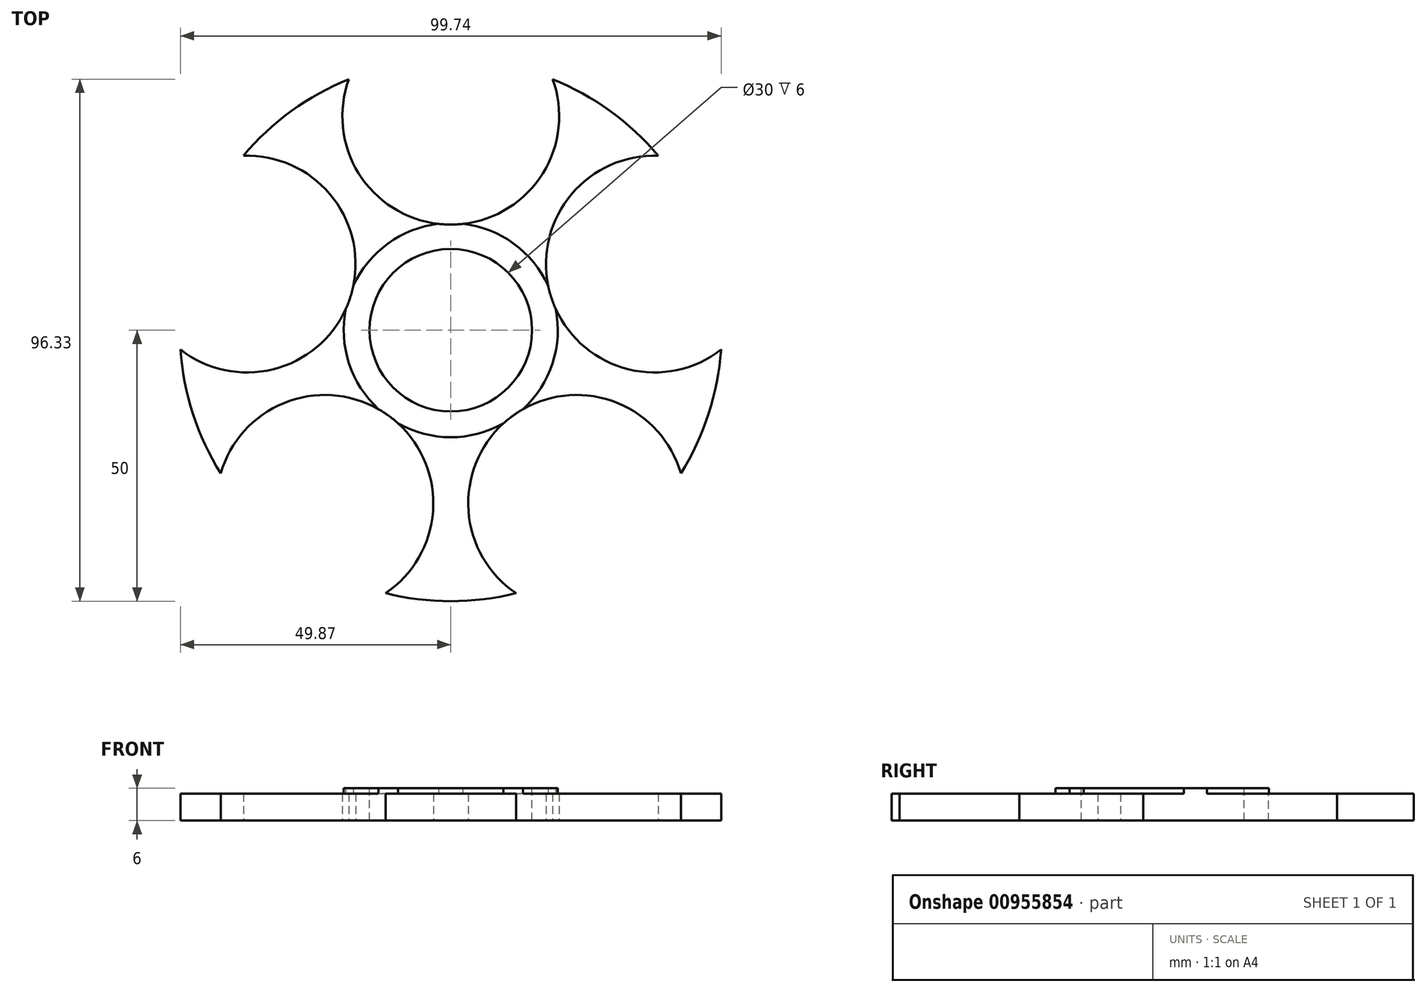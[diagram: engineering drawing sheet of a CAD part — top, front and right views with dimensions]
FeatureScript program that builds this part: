
annotation { "Feature Type Name" : "Feature", "Feature Type Description" : "" }
export const myFeature = defineFeature(function(context is Context, id is Id, definition is map)
    precondition{}
    {
        {
            var Q0;
            Q0=qCreatedBy(makeId("Top.planeOp"),FACE);
            var sketch = newSketch(context, id + "F0", { "sketchPlane" : qUnion([Q0])});
            skCircle(sketch, "E0.cCircle", {"center": v(0, 0) * mm, "radius": 39.5 * mm, "construction": true});
            skLineSegment(sketch, "E0.0", {"start": v(37.57, 12.2) * mm, "end": v(23.22, -31.96) * mm});
            skLineSegment(sketch, "E0.1", {"start": v(23.22, -31.96) * mm, "end": v(-23.22, -31.96) * mm});
            skLineSegment(sketch, "E0.2", {"start": v(-23.22, -31.96) * mm, "end": v(-37.57, 12.2) * mm});
            skLineSegment(sketch, "E0.3", {"start": v(-37.57, 12.2) * mm, "end": v(0, 39.5) * mm});
            skLineSegment(sketch, "E0.4", {"start": v(0, 39.5) * mm, "end": v(37.57, 12.2) * mm});
            skCircle(sketch, "E1", {"center": v(0, 39.5) * mm, "radius": 20 * mm});
            skCircle(sketch, "E2", {"center": v(37.57, 12.2) * mm, "radius": 20 * mm});
            skCircle(sketch, "E3", {"center": v(0, 0) * mm, "radius": 60 * mm});
            skCircle(sketch, "E4", {"center": v(-23.22, -31.96) * mm, "radius": 20 * mm});
            skCircle(sketch, "E5", {"center": v(23.22, -31.96) * mm, "radius": 20 * mm});
            skCircle(sketch, "E6", {"center": v(-37.57, 12.2) * mm, "radius": 20 * mm});
            skSolve(sketch);
        }
        {
            var Q0;
            Q0=makeQuery(id+"F0.imprint","IMPRINT",FACE,{"disambiguationData":[TD([[makeQuery(id+"F0.imprint","IMPRINT",EDGE,{"derivedFrom":sQuery(id+"F0.wireOp",EDGE,"E3")}),1.0]])]});
            var Q1;
            {var subQ0=sQuery(id+"F0.wireOp",EDGE,"E0.3");var subQ1=sQuery(id+"F0.wireOp",EDGE,"E0.2");var subQ2=makeQuery(id+"F0.imprint","INTERSECT",VERTEX,{"derivedFrom":[subQ1,subQ0]});Q1=makeQuery(id+"F0.imprint","IMPRINT",FACE,{"disambiguationData":[TD([[makeQuery(id+"F0.imprint","IMPRINT",EDGE,{"disambiguationData":[TD([[subQ2,1.0]])],"derivedFrom":subQ1}),1.0]])]});}
            var Q2;
            {var subQ0=sQuery(id+"F0.wireOp",EDGE,"E0.3");var subQ1=sQuery(id+"F0.wireOp",EDGE,"E0.2");var subQ2=makeQuery(id+"F0.imprint","INTERSECT",VERTEX,{"derivedFrom":[subQ1,subQ0]});Q2=makeQuery(id+"F0.imprint","IMPRINT",FACE,{"disambiguationData":[TD([[makeQuery(id+"F0.imprint","IMPRINT",EDGE,{"disambiguationData":[TD([[subQ2,1.0]])],"derivedFrom":subQ1}),-1.0]])]});}
            var Q3;
            {var subQ0=sQuery(id+"F0.wireOp",EDGE,"E0.2");var subQ1=sQuery(id+"F0.wireOp",EDGE,"E0.1");var subQ2=makeQuery(id+"F0.imprint","INTERSECT",VERTEX,{"derivedFrom":[subQ1,subQ0]});Q3=makeQuery(id+"F0.imprint","IMPRINT",FACE,{"disambiguationData":[TD([[makeQuery(id+"F0.imprint","IMPRINT",EDGE,{"disambiguationData":[TD([[subQ2,1.0]])],"derivedFrom":subQ1}),1.0]])]});}
            var Q4;
            {var subQ0=sQuery(id+"F0.wireOp",EDGE,"E0.2");var subQ1=sQuery(id+"F0.wireOp",EDGE,"E0.1");var subQ2=makeQuery(id+"F0.imprint","INTERSECT",VERTEX,{"derivedFrom":[subQ1,subQ0]});Q4=makeQuery(id+"F0.imprint","IMPRINT",FACE,{"disambiguationData":[TD([[makeQuery(id+"F0.imprint","IMPRINT",EDGE,{"disambiguationData":[TD([[subQ2,1.0]])],"derivedFrom":subQ1}),-1.0]])]});}
            var Q5;
            {var subQ0=sQuery(id+"F0.wireOp",EDGE,"E0.1");var subQ1=sQuery(id+"F0.wireOp",EDGE,"E0.0");var subQ2=makeQuery(id+"F0.imprint","INTERSECT",VERTEX,{"derivedFrom":[subQ1,subQ0]});Q5=makeQuery(id+"F0.imprint","IMPRINT",FACE,{"disambiguationData":[TD([[makeQuery(id+"F0.imprint","IMPRINT",EDGE,{"disambiguationData":[TD([[subQ2,1.0]])],"derivedFrom":subQ1}),1.0]])]});}
            var Q6;
            {var subQ0=sQuery(id+"F0.wireOp",EDGE,"E0.1");var subQ1=sQuery(id+"F0.wireOp",EDGE,"E0.0");var subQ2=makeQuery(id+"F0.imprint","INTERSECT",VERTEX,{"derivedFrom":[subQ1,subQ0]});Q6=makeQuery(id+"F0.imprint","IMPRINT",FACE,{"disambiguationData":[TD([[makeQuery(id+"F0.imprint","IMPRINT",EDGE,{"disambiguationData":[TD([[subQ2,1.0]])],"derivedFrom":subQ1}),-1.0]])]});}
            var Q7;
            {var subQ15=sQuery(id+"F0.wireOp",EDGE,"E2");var subQ16=sQuery(id+"F0.wireOp",EDGE,"E0.0");var subQ17=makeQuery(id+"F0.imprint","INTERSECT",VERTEX,{"derivedFrom":[subQ16,subQ15]});Q7=makeQuery(id+"F0.imprint","IMPRINT",FACE,{"disambiguationData":[TD([[makeQuery(id+"F0.imprint","IMPRINT",EDGE,{"disambiguationData":[TD([[subQ17,-1.0]])],"derivedFrom":subQ16}),-1.0]])]});}
            var Q8;
            {var subQ0=sQuery(id+"F0.wireOp",EDGE,"E0.4");var subQ1=sQuery(id+"F0.wireOp",EDGE,"E0.0");var subQ2=makeQuery(id+"F0.imprint","INTERSECT",VERTEX,{"derivedFrom":[subQ1,subQ0]});Q8=makeQuery(id+"F0.imprint","IMPRINT",FACE,{"disambiguationData":[TD([[makeQuery(id+"F0.imprint","IMPRINT",EDGE,{"disambiguationData":[TD([[subQ2,-1.0]])],"derivedFrom":subQ1}),-1.0]])]});}
            var Q9;
            {var subQ0=sQuery(id+"F0.wireOp",EDGE,"E0.4");var subQ1=sQuery(id+"F0.wireOp",EDGE,"E0.0");var subQ2=makeQuery(id+"F0.imprint","INTERSECT",VERTEX,{"derivedFrom":[subQ1,subQ0]});Q9=makeQuery(id+"F0.imprint","IMPRINT",FACE,{"disambiguationData":[TD([[makeQuery(id+"F0.imprint","IMPRINT",EDGE,{"disambiguationData":[TD([[subQ2,-1.0]])],"derivedFrom":subQ1}),1.0]])]});}
            var Q10;
            {var subQ0=sQuery(id+"F0.wireOp",EDGE,"E0.4");var subQ1=sQuery(id+"F0.wireOp",EDGE,"E0.3");var subQ2=makeQuery(id+"F0.imprint","INTERSECT",VERTEX,{"derivedFrom":[subQ1,subQ0]});Q10=makeQuery(id+"F0.imprint","IMPRINT",FACE,{"disambiguationData":[TD([[makeQuery(id+"F0.imprint","IMPRINT",EDGE,{"disambiguationData":[TD([[subQ2,1.0]])],"derivedFrom":subQ1}),-1.0]])]});}
            var Q11;
            {var subQ0=sQuery(id+"F0.wireOp",EDGE,"E0.4");var subQ1=sQuery(id+"F0.wireOp",EDGE,"E0.3");var subQ2=makeQuery(id+"F0.imprint","INTERSECT",VERTEX,{"derivedFrom":[subQ1,subQ0]});Q11=makeQuery(id+"F0.imprint","IMPRINT",FACE,{"disambiguationData":[TD([[makeQuery(id+"F0.imprint","IMPRINT",EDGE,{"disambiguationData":[TD([[subQ2,1.0]])],"derivedFrom":subQ1}),1.0]])]});}
            extrude(context, id + "F1", {"entities" : qUnion([Q0, Q1, Q2, Q3, Q4, Q5, Q6, Q7, Q8, Q9, Q10, Q11]), "depth" : 5 * mm, "offsetDistance" : 25 * mm});
        }
        {
            var Q0;
            Q0=makeQuery(id+"F1.opExtrude","CAP_FACE",FACE,{"disambiguationData":[OSD([sQuery(id+"F0.wireOp",EDGE,"E3")])],"isStart":false});
            var sketch = newSketch(context, id + "F2", { "sketchPlane" : qUnion([Q0])});
            skCircle(sketch, "E7", {"center": v(0, 0) * mm, "radius": 19.75 * mm});
            skSolve(sketch);
        }
        {
            var Q0;
            Q0=makeQuery(id+"F2.imprint","IMPRINT",FACE,{"disambiguationData":[TD([[makeQuery(id+"F2.imprint","IMPRINT",EDGE,{"derivedFrom":sQuery(id+"F2.wireOp",EDGE,"E7")}),1.0]])]});
            extrude(context, id + "F3", {"entities" : qUnion([Q0]), "operationType" : NewBodyOperationType.ADD, "depth" : 1 * mm, "offsetDistance" : 25 * mm});
        }
        {
            var Q0;
            {var subQ0=sQuery(id+"F0.wireOp",EDGE,"E0.2");var subQ1=sQuery(id+"F0.wireOp",EDGE,"E0.1");var subQ2=makeQuery(id+"F0.imprint","INTERSECT",VERTEX,{"derivedFrom":[subQ1,subQ0]});Q0=makeQuery(id+"F0.imprint","IMPRINT",FACE,{"disambiguationData":[TD([[makeQuery(id+"F0.imprint","IMPRINT",EDGE,{"disambiguationData":[TD([[subQ2,1.0]])],"derivedFrom":subQ1}),1.0]])]});}
            var Q1;
            {var subQ0=sQuery(id+"F0.wireOp",EDGE,"E0.2");var subQ1=sQuery(id+"F0.wireOp",EDGE,"E0.1");var subQ2=makeQuery(id+"F0.imprint","INTERSECT",VERTEX,{"derivedFrom":[subQ1,subQ0]});Q1=makeQuery(id+"F0.imprint","IMPRINT",FACE,{"disambiguationData":[TD([[makeQuery(id+"F0.imprint","IMPRINT",EDGE,{"disambiguationData":[TD([[subQ2,1.0]])],"derivedFrom":subQ1}),-1.0]])]});}
            var Q2;
            {var subQ0=sQuery(id+"F0.wireOp",EDGE,"E0.1");var subQ1=sQuery(id+"F0.wireOp",EDGE,"E0.0");var subQ2=makeQuery(id+"F0.imprint","INTERSECT",VERTEX,{"derivedFrom":[subQ1,subQ0]});Q2=makeQuery(id+"F0.imprint","IMPRINT",FACE,{"disambiguationData":[TD([[makeQuery(id+"F0.imprint","IMPRINT",EDGE,{"disambiguationData":[TD([[subQ2,1.0]])],"derivedFrom":subQ1}),1.0]])]});}
            var Q3;
            {var subQ0=sQuery(id+"F0.wireOp",EDGE,"E0.1");var subQ1=sQuery(id+"F0.wireOp",EDGE,"E0.0");var subQ2=makeQuery(id+"F0.imprint","INTERSECT",VERTEX,{"derivedFrom":[subQ1,subQ0]});Q3=makeQuery(id+"F0.imprint","IMPRINT",FACE,{"disambiguationData":[TD([[makeQuery(id+"F0.imprint","IMPRINT",EDGE,{"disambiguationData":[TD([[subQ2,1.0]])],"derivedFrom":subQ1}),-1.0]])]});}
            var Q4;
            {var subQ0=sQuery(id+"F0.wireOp",EDGE,"E0.4");var subQ1=sQuery(id+"F0.wireOp",EDGE,"E0.0");var subQ2=makeQuery(id+"F0.imprint","INTERSECT",VERTEX,{"derivedFrom":[subQ1,subQ0]});Q4=makeQuery(id+"F0.imprint","IMPRINT",FACE,{"disambiguationData":[TD([[makeQuery(id+"F0.imprint","IMPRINT",EDGE,{"disambiguationData":[TD([[subQ2,-1.0]])],"derivedFrom":subQ1}),1.0]])]});}
            var Q5;
            {var subQ0=sQuery(id+"F0.wireOp",EDGE,"E0.4");var subQ1=sQuery(id+"F0.wireOp",EDGE,"E0.0");var subQ2=makeQuery(id+"F0.imprint","INTERSECT",VERTEX,{"derivedFrom":[subQ1,subQ0]});Q5=makeQuery(id+"F0.imprint","IMPRINT",FACE,{"disambiguationData":[TD([[makeQuery(id+"F0.imprint","IMPRINT",EDGE,{"disambiguationData":[TD([[subQ2,-1.0]])],"derivedFrom":subQ1}),-1.0]])]});}
            var Q6;
            {var subQ0=sQuery(id+"F0.wireOp",EDGE,"E0.4");var subQ1=sQuery(id+"F0.wireOp",EDGE,"E0.3");var subQ2=makeQuery(id+"F0.imprint","INTERSECT",VERTEX,{"derivedFrom":[subQ1,subQ0]});Q6=makeQuery(id+"F0.imprint","IMPRINT",FACE,{"disambiguationData":[TD([[makeQuery(id+"F0.imprint","IMPRINT",EDGE,{"disambiguationData":[TD([[subQ2,1.0]])],"derivedFrom":subQ1}),-1.0]])]});}
            var Q7;
            {var subQ0=sQuery(id+"F0.wireOp",EDGE,"E0.4");var subQ1=sQuery(id+"F0.wireOp",EDGE,"E0.3");var subQ2=makeQuery(id+"F0.imprint","INTERSECT",VERTEX,{"derivedFrom":[subQ1,subQ0]});Q7=makeQuery(id+"F0.imprint","IMPRINT",FACE,{"disambiguationData":[TD([[makeQuery(id+"F0.imprint","IMPRINT",EDGE,{"disambiguationData":[TD([[subQ2,1.0]])],"derivedFrom":subQ1}),1.0]])]});}
            var Q8;
            {var subQ0=sQuery(id+"F0.wireOp",EDGE,"E0.3");var subQ1=sQuery(id+"F0.wireOp",EDGE,"E0.2");var subQ2=makeQuery(id+"F0.imprint","INTERSECT",VERTEX,{"derivedFrom":[subQ1,subQ0]});Q8=makeQuery(id+"F0.imprint","IMPRINT",FACE,{"disambiguationData":[TD([[makeQuery(id+"F0.imprint","IMPRINT",EDGE,{"disambiguationData":[TD([[subQ2,1.0]])],"derivedFrom":subQ1}),1.0]])]});}
            var Q9;
            {var subQ0=sQuery(id+"F0.wireOp",EDGE,"E0.3");var subQ1=sQuery(id+"F0.wireOp",EDGE,"E0.2");var subQ2=makeQuery(id+"F0.imprint","INTERSECT",VERTEX,{"derivedFrom":[subQ1,subQ0]});Q9=makeQuery(id+"F0.imprint","IMPRINT",FACE,{"disambiguationData":[TD([[makeQuery(id+"F0.imprint","IMPRINT",EDGE,{"disambiguationData":[TD([[subQ2,1.0]])],"derivedFrom":subQ1}),-1.0]])]});}
            extrude(context, id + "F4", {"entities" : qUnion([Q0, Q1, Q2, Q3, Q4, Q5, Q6, Q7, Q8, Q9]), "operationType" : NewBodyOperationType.REMOVE, "depth" : 25 * mm, "offsetDistance" : 25 * mm});
        }
        {
            var Q0;
            Q0=makeQuery(id+"F0.imprint","IMPRINT",FACE,{"disambiguationData":[TD([[makeQuery(id+"F0.imprint","IMPRINT",EDGE,{"derivedFrom":sQuery(id+"F0.wireOp",EDGE,"E3")}),1.0]])]});
            var sketch = newSketch(context, id + "F5", { "sketchPlane" : qUnion([Q0])});
            skCircle(sketch, "E8", {"center": v(0, 0) * mm, "radius": 50 * mm});
            skSolve(sketch);
        }
        {
            var Q0;
            Q0=makeQuery(id+"F5.imprint","IMPRINT",FACE,{"disambiguationData":[TD([[makeQuery(id+"F5.imprint","IMPRINT",EDGE,{"derivedFrom":makeQuery(id+"F0.imprint","IMPRINT",EDGE,{"derivedFrom":sQuery(id+"F0.wireOp",EDGE,"E3")})}),1.0]])]});
            extrude(context, id + "F6", {"entities" : qUnion([Q0]), "operationType" : NewBodyOperationType.REMOVE, "depth" : 25 * mm, "offsetDistance" : 25 * mm});
        }
        {
            var Q0;
            Q0=makeQuery(id+"F3.opExtrude","CAP_FACE",FACE,{"disambiguationData":[OSD([sQuery(id+"F2.wireOp",EDGE,"E7")])],"isStart":false});
            var sketch = newSketch(context, id + "F7", { "sketchPlane" : qUnion([Q0])});
            skCircle(sketch, "E9", {"center": v(0, 0) * mm, "radius": 15 * mm});
            skSolve(sketch);
        }
        {
            var Q0;
            Q0=makeQuery(id+"F7.imprint","IMPRINT",FACE,{"disambiguationData":[TD([[makeQuery(id+"F7.imprint","IMPRINT",EDGE,{"derivedFrom":sQuery(id+"F7.wireOp",EDGE,"E9")}),1.0]])]});
            extrude(context, id + "F8", {"entities" : qUnion([Q0]), "operationType" : NewBodyOperationType.REMOVE, "oppositeDirection" : true, "depth" : 25 * mm, "offsetDistance" : 25 * mm});
        }
    });
